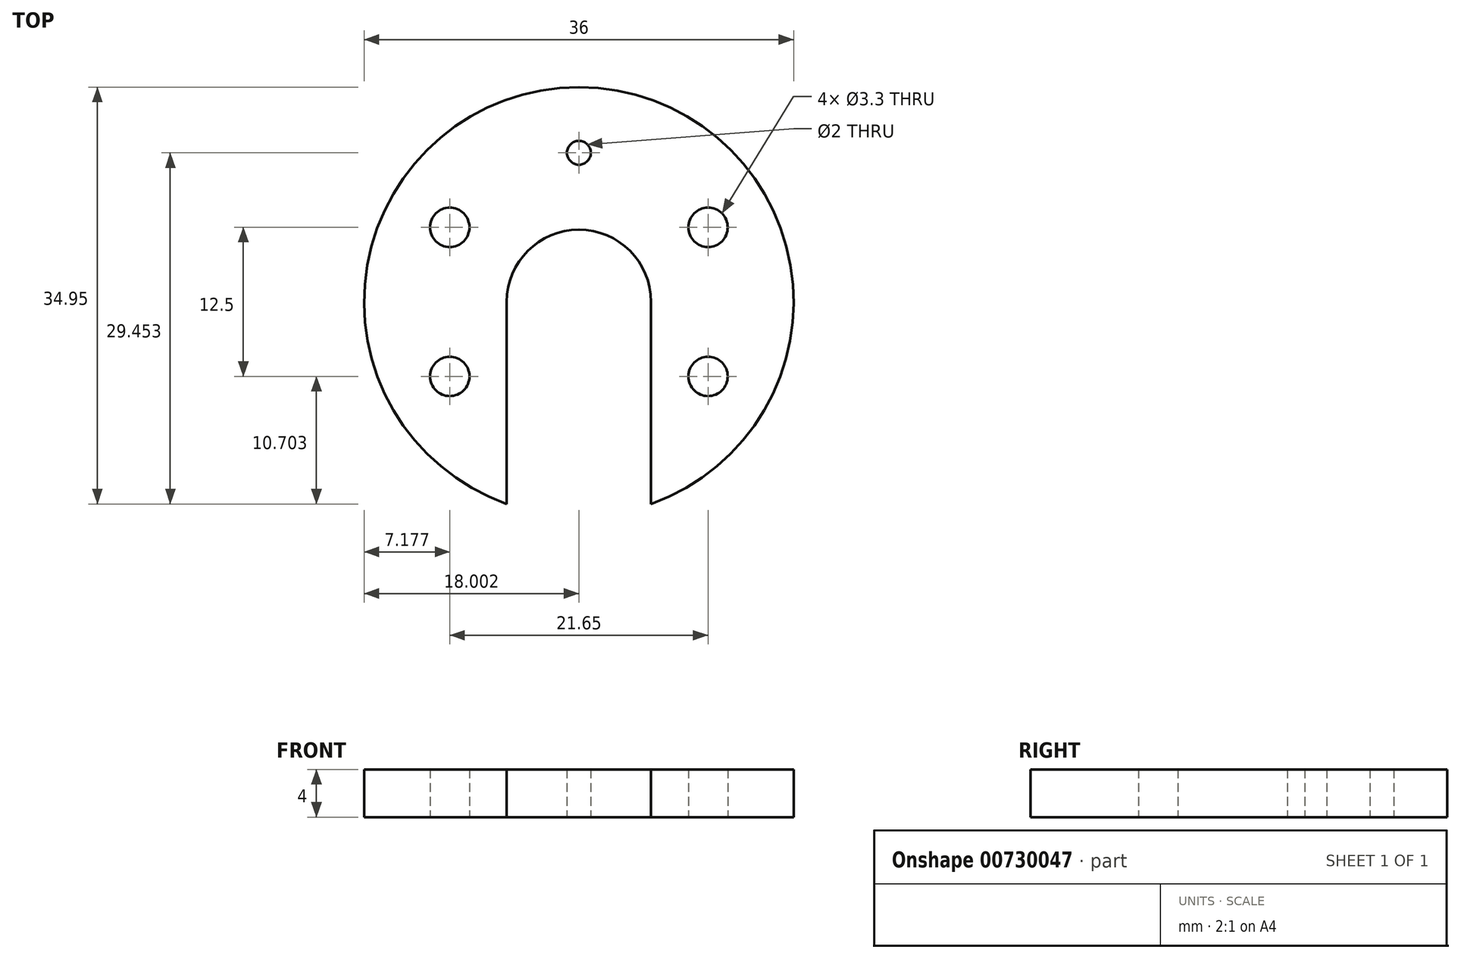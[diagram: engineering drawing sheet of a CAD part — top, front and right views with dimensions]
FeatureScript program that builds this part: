
annotation { "Feature Type Name" : "Feature", "Feature Type Description" : "" }
export const myFeature = defineFeature(function(context is Context, id is Id, definition is map)
    precondition{}
    {
        {
            var Q0;
            Q0=qCreatedBy(makeId("Top.planeOp"),FACE);
            var sketch = newSketch(context, id + "F0", { "sketchPlane" : qUnion([Q0])});
            skCircle(sketch, "E0", {"center": v(-39, 40.52) * mm, "radius": 1.65 * mm});
            skCircle(sketch, "E1", {"center": v(-17.34, 40.52) * mm, "radius": 1.65 * mm});
            skCircle(sketch, "E2", {"center": v(-39, 28.02) * mm, "radius": 1.65 * mm});
            skCircle(sketch, "E3", {"center": v(-17.34, 28.02) * mm, "radius": 1.65 * mm});
            skCircle(sketch, "E4", {"center": v(-28.17, 34.27) * mm, "radius": 18 * mm});
            skCircle(sketch, "E5", {"center": v(-28.17, 34.27) * mm, "radius": 6.05 * mm});
            skPoint(sketch, "E6", {"position": v(-34.22, 34.27) * mm});
            skPoint(sketch, "E7", {"position": v(-22.12, 34.27) * mm});
            skPoint(sketch, "E8", {"position": v(-22.12, 17.32) * mm});
            skPoint(sketch, "E9", {"position": v(-34.22, 17.32) * mm});
            skPoint(sketch, "E10", {"position": v(-1.92, 43.93) * mm});
            skLineSegment(sketch, "E11", {"start": v(-34.22, 34.27) * mm, "end": v(-34.22, 17.32) * mm});
            skLineSegment(sketch, "E12", {"start": v(-22.12, 34.27) * mm, "end": v(-22.12, 17.32) * mm});
            skCircle(sketch, "E13", {"center": v(-28.17, 46.77) * mm, "radius": 1 * mm});
            skSolve(sketch);
        }
        {
            var Q0;
            Q0=makeQuery(id+"F0.imprint","IMPRINT",FACE,{"disambiguationData":[TD([[makeQuery(id+"F0.imprint","IMPRINT",EDGE,{"derivedFrom":sQuery(id+"F0.wireOp",EDGE,"E0")}),-1.0]])]});
            extrude(context, id + "F1", {"entities" : qUnion([Q0]), "depth" : 4 * mm, "offsetDistance" : 25 * mm});
        }
    });
